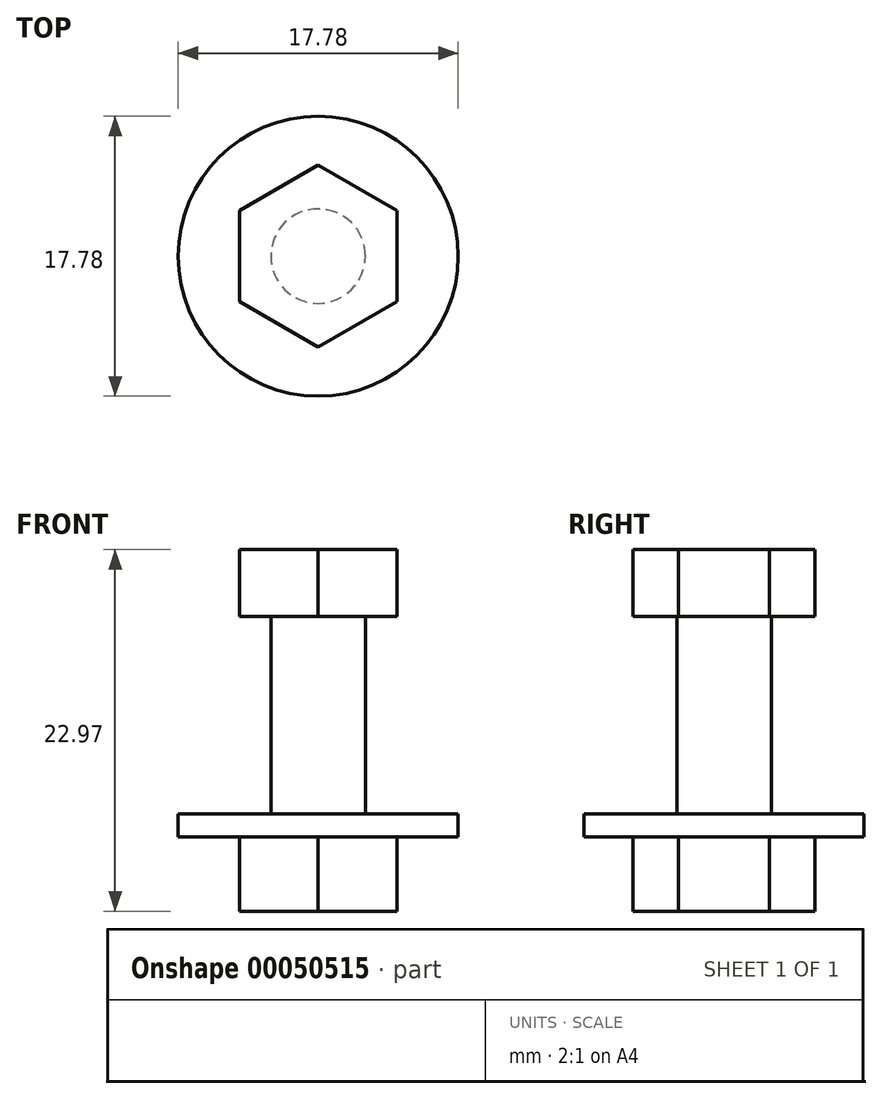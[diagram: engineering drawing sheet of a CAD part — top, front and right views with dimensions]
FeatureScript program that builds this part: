
annotation { "Feature Type Name" : "Feature", "Feature Type Description" : "" }
export const myFeature = defineFeature(function(context is Context, id is Id, definition is map)
    precondition{}
    {
        {
            var Q0;
            Q0=qCreatedBy(makeId("Top.planeOp"),FACE);
            var sketch = newSketch(context, id + "F0", { "sketchPlane" : qUnion([Q0])});
            skCircle(sketch, "E0", {"center": v(0, 0) * mm, "radius": 3 * mm});
            skSolve(sketch);
        }
        {
            var Q0;
            Q0=qSketchRegion(id+"F0",true);
            extrude(context, id + "F1", {"entities" : qUnion([Q0]), "oppositeDirection" : true, "depth" : 20 * mm});
        }
        {
            var Q0;
            Q0=makeQuery(id+"F1.opExtrude","CAP_FACE",FACE,{"disambiguationData":[OSD([sQuery(id+"F0.wireOp",EDGE,"E0")])],"isStart":true});
            var sketch = newSketch(context, id + "F2", { "sketchPlane" : qUnion([Q0])});
            skCircle(sketch, "E1.cCircle", {"center": v(0, 0) * mm, "radius": 5 * mm, "construction": true});
            skLineSegment(sketch, "E1.0", {"start": v(0, 5.77) * mm, "end": v(5, 2.89) * mm});
            skLineSegment(sketch, "E1.1", {"start": v(5, 2.89) * mm, "end": v(5, -2.89) * mm});
            skLineSegment(sketch, "E1.2", {"start": v(5, -2.89) * mm, "end": v(0, -5.77) * mm});
            skLineSegment(sketch, "E1.3", {"start": v(0, -5.77) * mm, "end": v(-5, -2.89) * mm});
            skLineSegment(sketch, "E1.4", {"start": v(-5, -2.89) * mm, "end": v(-5, 2.89) * mm});
            skLineSegment(sketch, "E1.5", {"start": v(-5, 2.89) * mm, "end": v(0, 5.77) * mm});
            skPoint(sketch, "E1.0.midPoint", {"position": v(2.5, 4.33) * mm});
            skSolve(sketch);
        }
        {
            var Q0;
            Q0=qSketchRegion(id+"F2",true);
            extrude(context, id + "F3", {"entities" : qUnion([Q0]), "operationType" : NewBodyOperationType.ADD, "depth" : 4.24 * mm});
        }
        {
            var Q0;
            Q0=makeQuery(id+"F1.opExtrude","CAP_FACE",FACE,{"disambiguationData":[OSD([sQuery(id+"F0.wireOp",EDGE,"E0")])],"isStart":false});
            var sketch = newSketch(context, id + "F4", { "sketchPlane" : qUnion([Q0])});
            skCircle(sketch, "E2.cCircle", {"center": v(0, 0) * mm, "radius": 5 * mm, "construction": true});
            skLineSegment(sketch, "E2.0", {"start": v(0, 5.77) * mm, "end": v(5, 2.89) * mm});
            skLineSegment(sketch, "E2.1", {"start": v(5, 2.89) * mm, "end": v(5, -2.89) * mm});
            skLineSegment(sketch, "E2.2", {"start": v(5, -2.89) * mm, "end": v(0, -5.77) * mm});
            skLineSegment(sketch, "E2.3", {"start": v(0, -5.77) * mm, "end": v(-5, -2.89) * mm});
            skLineSegment(sketch, "E2.4", {"start": v(-5, -2.89) * mm, "end": v(-5, 2.89) * mm});
            skLineSegment(sketch, "E2.5", {"start": v(-5, 2.89) * mm, "end": v(0, 5.77) * mm});
            skPoint(sketch, "E2.0.midPoint", {"position": v(2.5, 4.33) * mm});
            skSolve(sketch);
        }
        {
            var Q0;
            Q0=qSketchRegion(id+"F4",true);
            extrude(context, id + "F5", {"entities" : qUnion([Q0]), "operationType" : NewBodyOperationType.ADD, "oppositeDirection" : true, "depth" : 6 * mm});
        }
        {
            var Q0;
            Q0=makeQuery(id+"F5.opExtrude","CAP_FACE",FACE,{"disambiguationData":[OSD([sQuery(id+"F4.wireOp",EDGE,"E2.0"),sQuery(id+"F4.wireOp",EDGE,"E2.1"),sQuery(id+"F4.wireOp",EDGE,"E2.2"),sQuery(id+"F4.wireOp",EDGE,"E2.3"),sQuery(id+"F4.wireOp",EDGE,"E2.4"),sQuery(id+"F4.wireOp",EDGE,"E2.5")])],"isStart":false});
            var sketch = newSketch(context, id + "F6", { "sketchPlane" : qUnion([Q0])});
            skCircle(sketch, "E3", {"center": v(0, 0) * mm, "radius": 8.9 * mm});
            skSolve(sketch);
        }
        {
            var Q0;
            Q0=qSketchRegion(id+"F6",true);
            extrude(context, id + "F7", {"entities" : qUnion([Q0]), "operationType" : NewBodyOperationType.ADD, "depth" : 1.45 * mm});
        }
        {
            var Q0;
            Q0=makeQuery(id+"F5.boolean.opBoolean","MERGE",FACE,{"derivedFrom":[makeQuery(id+"F1.opExtrude","CAP_FACE",FACE,{"disambiguationData":[OSD([sQuery(id+"F0.wireOp",EDGE,"E0")])],"isStart":false}),makeQuery(id+"F5.opExtrude","CAP_FACE",FACE,{"disambiguationData":[OSD([sQuery(id+"F4.wireOp",EDGE,"E2.0"),sQuery(id+"F4.wireOp",EDGE,"E2.1"),sQuery(id+"F4.wireOp",EDGE,"E2.2"),sQuery(id+"F4.wireOp",EDGE,"E2.3"),sQuery(id+"F4.wireOp",EDGE,"E2.4"),sQuery(id+"F4.wireOp",EDGE,"E2.5")])],"isStart":true})]});
            var sketch = newSketch(context, id + "F8", { "sketchPlane" : qUnion([Q0])});
            skCircle(sketch, "E4", {"center": v(0, 0) * mm, "radius": 5.08 * mm});
            skLineSegment(sketch, "E5.0.0", {"start": v(5, 2.89) * mm, "end": v(0, 5.77) * mm});
            skLineSegment(sketch, "E5.0.1", {"start": v(0, 5.77) * mm, "end": v(-5, 2.89) * mm});
            skLineSegment(sketch, "E5.0.2", {"start": v(-5, 2.89) * mm, "end": v(-5, -2.89) * mm});
            skLineSegment(sketch, "E5.0.3", {"start": v(-5, -2.89) * mm, "end": v(0, -5.77) * mm});
            skLineSegment(sketch, "E5.0.4", {"start": v(0, -5.77) * mm, "end": v(5, -2.89) * mm});
            skLineSegment(sketch, "E5.0.5", {"start": v(5, -2.89) * mm, "end": v(5, 2.89) * mm});
            skSolve(sketch);
        }
        {
            var Q0;
            Q0=qSketchRegion(id+"F8",true);
            extrude(context, id + "F9", {"entities" : qUnion([Q0]), "operationType" : NewBodyOperationType.REMOVE, "oppositeDirection" : true, "depth" : 1.27 * mm});
        }
    });
